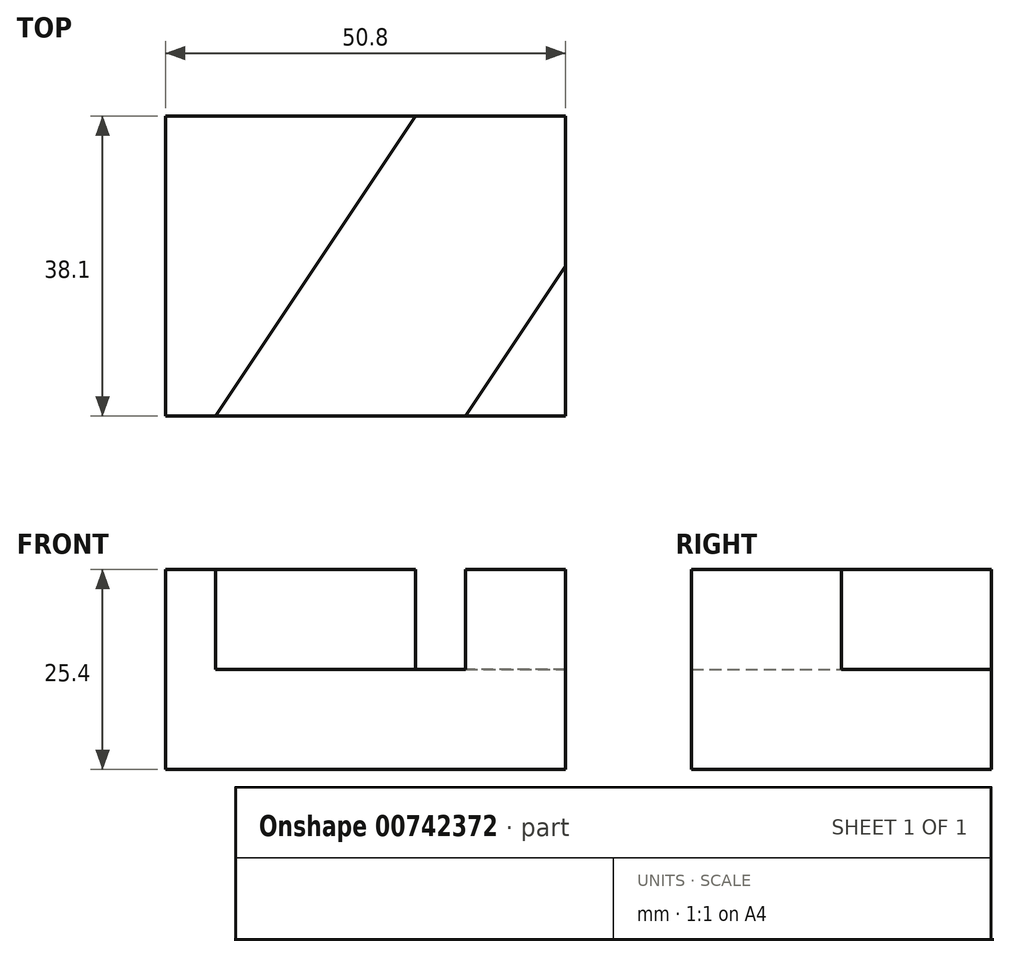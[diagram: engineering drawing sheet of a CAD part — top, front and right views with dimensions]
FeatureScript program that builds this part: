
annotation { "Feature Type Name" : "Feature", "Feature Type Description" : "" }
export const myFeature = defineFeature(function(context is Context, id is Id, definition is map)
    precondition{}
    {
        {
            var Q0;
            Q0=qCreatedBy(makeId("Front.planeOp"),FACE);
            var sketch = newSketch(context, id + "F0", { "sketchPlane" : qUnion([Q0])});
            skLineSegment(sketch, "E0.bottom", {"start": v(0, 0) * mm, "end": v(-50.8, 0) * mm});
            skLineSegment(sketch, "E0.top", {"start": v(0, 25.4) * mm, "end": v(-50.8, 25.4) * mm});
            skLineSegment(sketch, "E0.left", {"start": v(0, 0) * mm, "end": v(0, 25.4) * mm});
            skLineSegment(sketch, "E0.right", {"start": v(-50.8, 0) * mm, "end": v(-50.8, 25.4) * mm});
            skSolve(sketch);
        }
        {
            var Q0;
            Q0 = qSketchRegion(id + "F0", true);
            extrude(context, id + "F1", {"entities" : qUnion([Q0]), "depth" : 38.1 * mm, "offsetDistance" : 25.4 * mm});
        }
        {
            var Q0;
            Q0=makeQuery(id+"F1.opExtrude","SWEPT_FACE",FACE,{"disambiguationData":[OSD([sQuery(id+"F0.wireOp",EDGE,"E0.top")])]});
            var sketch = newSketch(context, id + "F2", { "sketchPlane" : qUnion([Q0])});
            skLineSegment(sketch, "E1", {"start": v(-44.45, -38.1) * mm, "end": v(-19.05, 0) * mm});
            skPoint(sketch, "E2", {"position": v(-25.4, 0) * mm});
            skLineSegment(sketch, "E3", {"start": v(-12.7, -38.1) * mm, "end": v(0, -19.05) * mm});
            skSolve(sketch);
        }
        {
            var Q0;
            {var subQ5=sQuery(id+"F2.wireOp",EDGE,"E1");Q0=makeQuery(id+"F2.imprint","IMPRINT",FACE,{"disambiguationData":[TD([[makeQuery(id+"F2.imprint","IMPRINT",EDGE,{"derivedFrom":subQ5}),-1.0]])]});}
            extrude(context, id + "F3", {"entities" : qUnion([Q0]), "operationType" : NewBodyOperationType.REMOVE, "oppositeDirection" : true, "depth" : 12.7 * mm, "offsetDistance" : 25.4 * mm});
        }
    });
